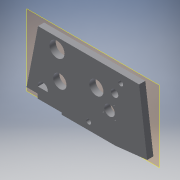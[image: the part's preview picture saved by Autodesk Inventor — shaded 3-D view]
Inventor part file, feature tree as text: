
AUTODESK INVENTOR PART (.ipt)
format: ipt  version: 2018 (Build 220112000, 112)  size: 146,432 bytes
history: native  units: in
note: dims shown in document units (in); Inventor stores cm internally (conversion verified against a paired STEP export)
features: other x5, extrude x2, sketch x2, plane x1, reference x1
ambient origin geometry x8: Origin, YZ Plane, XZ Plane, XY Plane, X Axis, Y Axis, Z Axis, Center Point
bodies: Solid1 (feature_tree)
feature tree (11):
  other  "Table"
  other  "Part11-01"
  other  "Part11-02"
  plane  "Work Plane1"
  extrude  "Extrusion1"  Depth=1.0in TaperAngle=0.0deg
  extrude  "Extrusion2"  [1 undecoded]
  sketch  "Sketch1"  dims[d0=1.0in d1=0.0in d3=1.0in d4=0.0in]
  reference  "Reference1"
  sketch  "Sketch2"
  other  "Lathe Model 2018.iam"
  other  "Gearbox:1"
note: 1 required parameter value undecoded (feature->parameter linkage not recoverable at this tier; creation-order binding heuristic only, values carry confidence <= 0.55)
